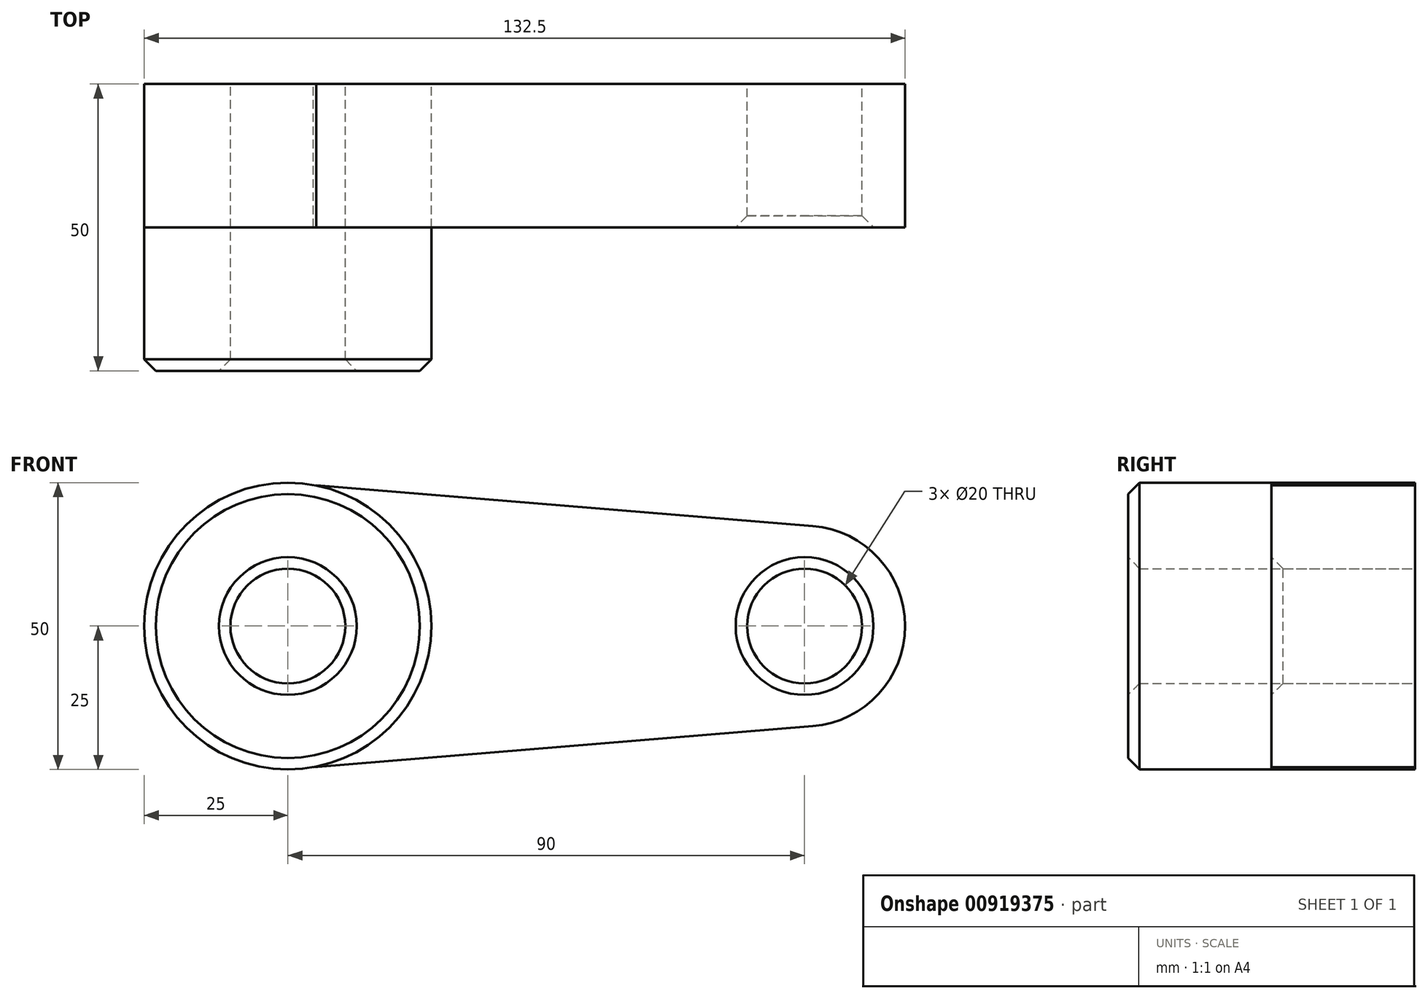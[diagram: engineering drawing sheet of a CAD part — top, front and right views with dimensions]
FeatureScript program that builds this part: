
annotation { "Feature Type Name" : "Feature", "Feature Type Description" : "" }
export const myFeature = defineFeature(function(context is Context, id is Id, definition is map)
    precondition{}
    {
        {
            var Q0;
            Q0=qCreatedBy(makeId("Front.planeOp"),FACE);
            var sketch = newSketch(context, id + "F0", { "sketchPlane" : qUnion([Q0])});
            skCircle(sketch, "E0", {"center": v(0, 0) * mm, "radius": 25 * mm});
            skCircle(sketch, "E1", {"center": v(90, 0) * mm, "radius": 17.5 * mm});
            skLineSegment(sketch, "E2", {"start": v(4.92, 24.51) * mm, "end": v(91.43, 17.44) * mm});
            skLineSegment(sketch, "E3", {"start": v(4.45, -24.6) * mm, "end": v(91.44, -17.44) * mm});
            skCircle(sketch, "E4", {"center": v(0, 0) * mm, "radius": 10 * mm});
            skCircle(sketch, "E5", {"center": v(90, 0) * mm, "radius": 10 * mm});
            skSolve(sketch);
        }
        {
            var Q0;
            Q0=makeQuery(id+"F0.imprint","IMPRINT",FACE,{"disambiguationData":[TD([[makeQuery(id+"F0.imprint","IMPRINT",EDGE,{"derivedFrom":sQuery(id+"F0.wireOp",EDGE,"E5")}),-1.0]])]});
            var Q1;
            {var subQ0=sQuery(id+"F0.wireOp",EDGE,"E2");Q1=makeQuery(id+"F0.imprint","IMPRINT",FACE,{"disambiguationData":[TD([[makeQuery(id+"F0.imprint","IMPRINT",EDGE,{"derivedFrom":subQ0}),-1.0]])]});}
            var Q2;
            Q2=makeQuery(id+"F0.imprint","IMPRINT",FACE,{"disambiguationData":[TD([[makeQuery(id+"F0.imprint","IMPRINT",EDGE,{"derivedFrom":sQuery(id+"F0.wireOp",EDGE,"E4")}),-1.0]])]});
            extrude(context, id + "F1", {"entities" : qUnion([Q0, Q1, Q2]), "depth" : 25 * mm, "offsetDistance" : 25 * mm});
        }
        {
            var Q0;
            Q0=makeQuery(id+"F0.imprint","IMPRINT",FACE,{"disambiguationData":[TD([[makeQuery(id+"F0.imprint","IMPRINT",EDGE,{"derivedFrom":sQuery(id+"F0.wireOp",EDGE,"E4")}),-1.0]])]});
            extrude(context, id + "F2", {"entities" : qUnion([Q0]), "depth" : 50 * mm, "offsetDistance" : 25 * mm});
        }
        {
            var Q0;
            Q0=makeQuery(id+"F2.opExtrude","CAP_EDGE",EDGE,{"disambiguationData":[OSD([sQuery(id+"F0.wireOp",EDGE,"E4")])],"isStart":false});
            var Q1;
            Q1=makeQuery(id+"F2.opExtrude","CAP_EDGE",EDGE,{"disambiguationData":[OSD([sQuery(id+"F0.wireOp",EDGE,"E0")])],"isStart":false});
            var Q2;
            Q2=makeQuery(id+"F1.opExtrude","CAP_EDGE",EDGE,{"disambiguationData":[OSD([sQuery(id+"F0.wireOp",EDGE,"E5")])],"isStart":false});
            chamfer(context, id + "F3", {"entities" : qUnion([Q0, Q1, Q2]), "width" : 2 * mm, "tangentPropagation" : true});
        }
    });
